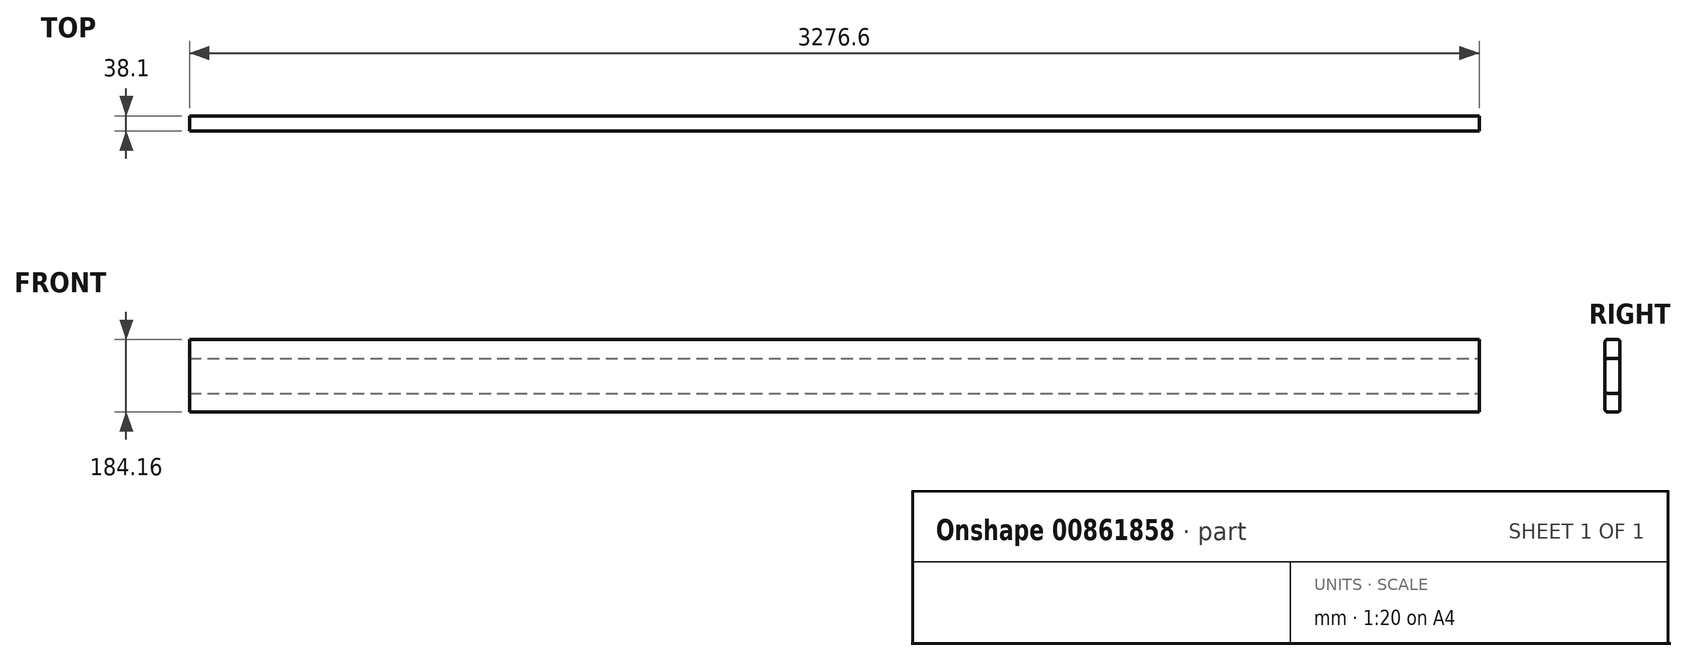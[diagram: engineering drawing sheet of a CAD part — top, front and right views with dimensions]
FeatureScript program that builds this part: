
annotation { "Feature Type Name" : "Feature", "Feature Type Description" : "" }
export const myFeature = defineFeature(function(context is Context, id is Id, definition is map)
    precondition{}
    {
        {
            var Q0;
            Q0=qCreatedBy(makeId("Front.planeOp"),FACE);
            var sketch = newSketch(context, id + "F0", { "sketchPlane" : qUnion([Q0])});
            skLineSegment(sketch, "E0.bottom", {"start": v(-1638.3, -44.45) * mm, "end": v(1638.3, -44.45) * mm});
            skLineSegment(sketch, "E0.top", {"start": v(-1638.3, 44.45) * mm, "end": v(1638.3, 44.45) * mm});
            skLineSegment(sketch, "E0.left", {"start": v(-1638.3, -44.45) * mm, "end": v(-1638.3, 44.45) * mm});
            skLineSegment(sketch, "E0.right", {"start": v(1638.3, -44.45) * mm, "end": v(1638.3, 44.45) * mm});
            skPoint(sketch, "E0.middle", {"position": v(0, 0) * mm});
            skSolve(sketch);
        }
        {
            var Q0;
            Q0=makeQuery(id+"F0.imprint","IMPRINT",FACE,{"disambiguationData":[TD([[makeQuery(id+"F0.imprint","IMPRINT",EDGE,{"derivedFrom":sQuery(id+"F0.wireOp",EDGE,"E0.bottom")}),1.0]])]});
            extrude(context, id + "F1", {"entities" : qUnion([Q0]), "endBound" : BoundingType.SYMMETRIC, "depth" : 38.1 * mm, "offsetDistance" : 25.4 * mm});
        }
        {
            var Q0;
            Q0=makeQuery(id+"F1.opExtrude","CAP_EDGE",EDGE,{"disambiguationData":[OSD([sQuery(id+"F0.wireOp",EDGE,"E0.top")])],"isStart":false});
            var Q1;
            Q1=makeQuery(id+"F1.opExtrude","CAP_EDGE",EDGE,{"disambiguationData":[OSD([sQuery(id+"F0.wireOp",EDGE,"E0.top")])],"isStart":true});
            var Q2;
            Q2=makeQuery(id+"F1.opExtrude","CAP_EDGE",EDGE,{"disambiguationData":[OSD([sQuery(id+"F0.wireOp",EDGE,"E0.bottom")])],"isStart":true});
            var Q3;
            Q3=makeQuery(id+"F1.opExtrude","CAP_EDGE",EDGE,{"disambiguationData":[OSD([sQuery(id+"F0.wireOp",EDGE,"E0.bottom")])],"isStart":false});
            fillet(context, id + "F2", {"entities" : qUnion([Q0, Q1, Q2, Q3]), "radius" : 6.35 * mm, "tangentPropagation" : true, "allowEdgeOverflow" : false});
        }
        {
            var Q0;
            Q0=qCreatedBy(makeId("Front.planeOp"),FACE);
            var sketch = newSketch(context, id + "F3", { "sketchPlane" : qUnion([Q0])});
            skLineSegment(sketch, "E1.bottom", {"start": v(-1638.3, -92.07) * mm, "end": v(1638.3, -92.07) * mm});
            skLineSegment(sketch, "E1.top", {"start": v(-1638.3, 92.07) * mm, "end": v(1638.3, 92.07) * mm});
            skLineSegment(sketch, "E1.left", {"start": v(-1638.3, -92.07) * mm, "end": v(-1638.3, 92.07) * mm});
            skLineSegment(sketch, "E1.right", {"start": v(1638.3, -92.07) * mm, "end": v(1638.3, 92.07) * mm});
            skPoint(sketch, "E1.middle", {"position": v(0, 0) * mm});
            skSolve(sketch);
        }
        {
            var Q0;
            Q0=makeQuery(id+"F3.imprint","IMPRINT",FACE,{"disambiguationData":[TD([[makeQuery(id+"F3.imprint","IMPRINT",EDGE,{"derivedFrom":sQuery(id+"F3.wireOp",EDGE,"E1.bottom")}),1.0]])]});
            extrude(context, id + "F4", {"entities" : qUnion([Q0]), "endBound" : BoundingType.SYMMETRIC, "depth" : 38.1 * mm, "offsetDistance" : 25.4 * mm});
        }
        {
            var Q0;
            Q0=makeQuery(id+"F4.opExtrude","CAP_EDGE",EDGE,{"disambiguationData":[OSD([sQuery(id+"F3.wireOp",EDGE,"E1.top")])],"isStart":false});
            var Q1;
            Q1=makeQuery(id+"F4.opExtrude","CAP_EDGE",EDGE,{"disambiguationData":[OSD([sQuery(id+"F3.wireOp",EDGE,"E1.top")])],"isStart":true});
            var Q2;
            Q2=makeQuery(id+"F4.opExtrude","CAP_EDGE",EDGE,{"disambiguationData":[OSD([sQuery(id+"F3.wireOp",EDGE,"E1.bottom")])],"isStart":false});
            var Q3;
            Q3=makeQuery(id+"F4.opExtrude","CAP_EDGE",EDGE,{"disambiguationData":[OSD([sQuery(id+"F3.wireOp",EDGE,"E1.bottom")])],"isStart":true});
            fillet(context, id + "F5", {"entities" : qUnion([Q0, Q1, Q2, Q3]), "radius" : 6.35 * mm, "tangentPropagation" : true, "allowEdgeOverflow" : false});
        }
    });
